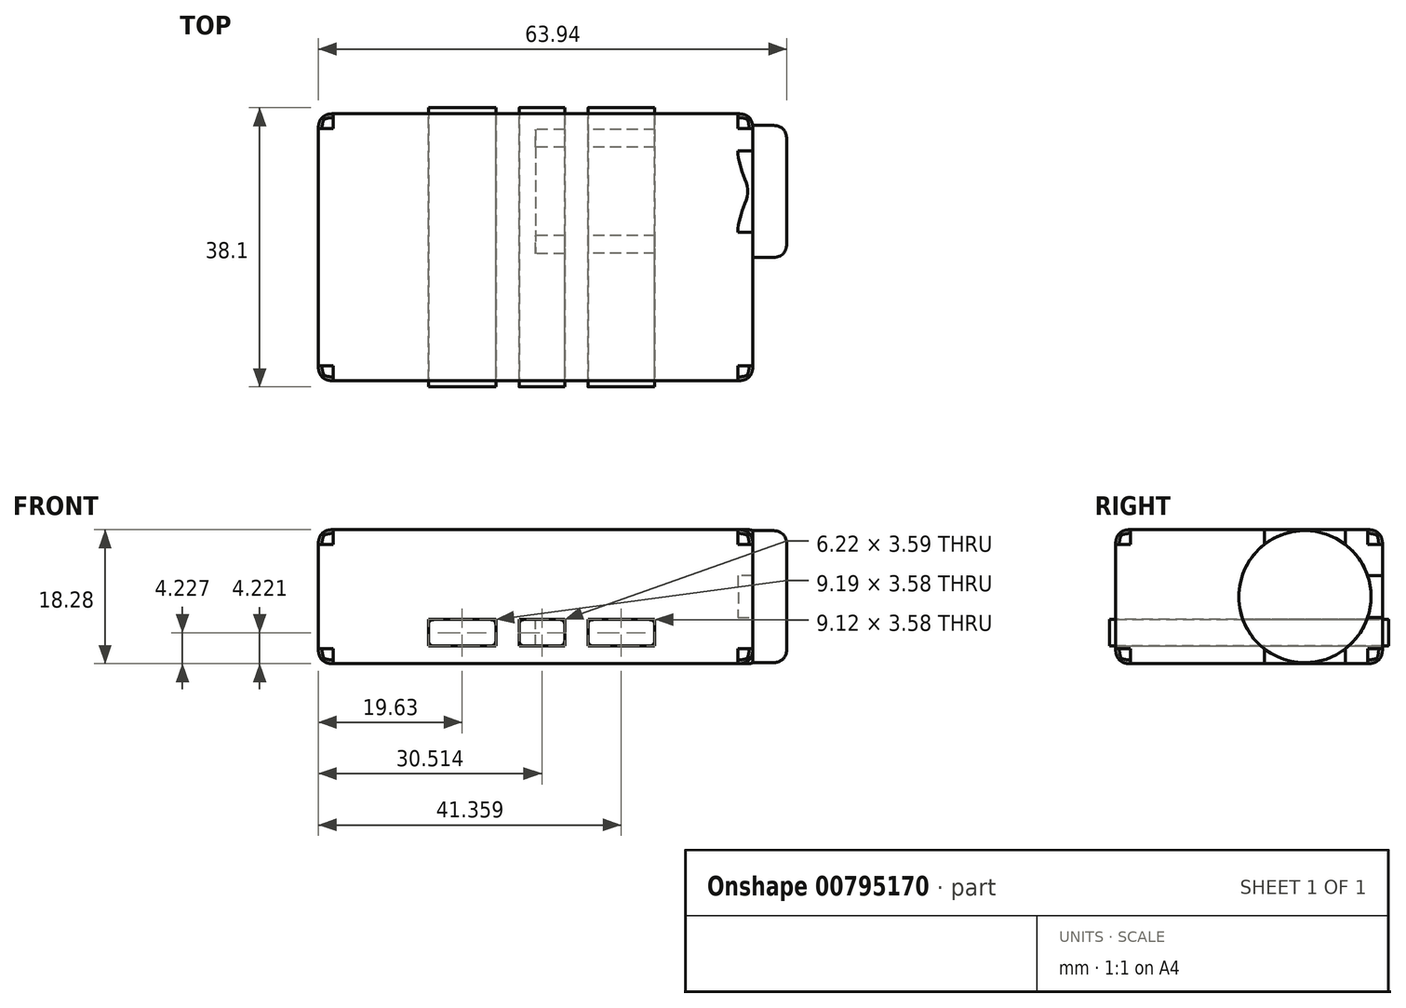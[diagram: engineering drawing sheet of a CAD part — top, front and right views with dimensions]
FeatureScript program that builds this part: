
annotation { "Feature Type Name" : "Feature", "Feature Type Description" : "" }
export const myFeature = defineFeature(function(context is Context, id is Id, definition is map)
    precondition{}
    {
        {
            var Q0;
            Q0=qCreatedBy(makeId("Front.planeOp"),FACE);
            var sketch = newSketch(context, id + "F0", { "sketchPlane" : qUnion([Q0])});
            skLineSegment(sketch, "E0.bottom", {"start": v(29.65, 9.14) * mm, "end": v(-29.65, 9.14) * mm});
            skLineSegment(sketch, "E0.top", {"start": v(29.65, -9.14) * mm, "end": v(-29.65, -9.14) * mm});
            skLineSegment(sketch, "E0.left", {"start": v(29.65, 9.14) * mm, "end": v(29.65, -9.14) * mm});
            skLineSegment(sketch, "E0.right", {"start": v(-29.65, 9.14) * mm, "end": v(-29.65, -9.14) * mm});
            skPoint(sketch, "E0.middle", {"position": v(0, 0) * mm});
            skLineSegment(sketch, "E1.left", {"start": v(29.65, 0) * mm, "end": v(29.65, 9.14) * mm});
            skLineSegment(sketch, "E2.bottom", {"start": v(7.15, -6.7) * mm, "end": v(16.27, -6.7) * mm});
            skLineSegment(sketch, "E2.top", {"start": v(7.15, -3.13) * mm, "end": v(16.27, -3.13) * mm});
            skLineSegment(sketch, "E2.left", {"start": v(7.15, -6.7) * mm, "end": v(7.15, -3.13) * mm});
            skLineSegment(sketch, "E2.right", {"start": v(16.27, -6.7) * mm, "end": v(16.27, -3.13) * mm});
            skLineSegment(sketch, "E3.left", {"start": v(7.15, -3.13) * mm, "end": v(7.15, -6.7) * mm});
            skLineSegment(sketch, "E4.bottom", {"start": v(3.98, -6.7) * mm, "end": v(-2.25, -6.7) * mm});
            skLineSegment(sketch, "E4.top", {"start": v(3.98, -3.12) * mm, "end": v(-2.25, -3.12) * mm});
            skLineSegment(sketch, "E4.left", {"start": v(3.98, -6.7) * mm, "end": v(3.98, -3.12) * mm});
            skLineSegment(sketch, "E4.right", {"start": v(-2.25, -6.7) * mm, "end": v(-2.25, -3.12) * mm});
            skLineSegment(sketch, "E5.bottom", {"start": v(-14.62, -6.7) * mm, "end": v(-5.42, -6.7) * mm});
            skLineSegment(sketch, "E5.top", {"start": v(-14.62, -3.13) * mm, "end": v(-5.42, -3.13) * mm});
            skLineSegment(sketch, "E5.left", {"start": v(-14.62, -6.7) * mm, "end": v(-14.62, -3.13) * mm});
            skLineSegment(sketch, "E5.right", {"start": v(-5.42, -6.7) * mm, "end": v(-5.42, -3.13) * mm});
            skSolve(sketch);
        }
        {
            var Q0;
            Q0=makeQuery(id+"F0.imprint","IMPRINT",FACE,{"disambiguationData":[TD([[makeQuery(id+"F0.imprint","IMPRINT",EDGE,{"derivedFrom":sQuery(id+"F0.wireOp",EDGE,"E0.bottom")}),1.0]])]});
            extrude(context, id + "F1", {"entities" : qUnion([Q0]), "endBound" : BoundingType.SYMMETRIC, "depth" : 36.42 * mm, "offsetDistance" : 25.4 * mm});
        }
        {
            var Q0;
            Q0=qCreatedBy(makeId("Right.planeOp"),FACE);
            var sketch = newSketch(context, id + "F2", { "sketchPlane" : qUnion([Q0])});
            skCircle(sketch, "E6", {"center": v(7.62, 0) * mm, "radius": 9.02 * mm});
            skSolve(sketch);
        }
        {
            var Q0;
            Q0 = qSketchRegion(id + "F2", true);
            extrude(context, id + "F3", {"entities" : qUnion([Q0]), "operationType" : NewBodyOperationType.ADD, "depth" : 34.3 * mm, "offsetDistance" : 25.4 * mm});
        }
        {
            var Q0;
            Q0=makeQuery(id+"F1.opExtrude","CAP_EDGE",EDGE,{"disambiguationData":[OSD([sQuery(id+"F0.wireOp",EDGE,"E0.bottom")])],"isStart":false});
            var Q1;
            Q1=makeQuery(id+"F1.opExtrude","CAP_EDGE",EDGE,{"disambiguationData":[OSD([sQuery(id+"F0.wireOp",EDGE,"E0.top")])],"isStart":false});
            var Q2;
            Q2=makeQuery(id+"F1.opExtrude","CAP_EDGE",EDGE,{"disambiguationData":[OSD([sQuery(id+"F0.wireOp",EDGE,"E0.left"),sQuery(id+"F0.wireOp",EDGE,"E1.left")])],"isStart":false});
            var Q3;
            Q3=makeQuery(id+"F1.opExtrude","SWEPT_EDGE",EDGE,{"disambiguationData":[OSD([sQuery(id+"F0.wireOp",EDGE,"E0.bottom"),sQuery(id+"F0.wireOp",EDGE,"E1.left")])]});
            var Q4;
            Q4=makeQuery(id+"F1.opExtrude","SWEPT_EDGE",EDGE,{"disambiguationData":[OSD([sQuery(id+"F0.wireOp",EDGE,"E0.top"),sQuery(id+"F0.wireOp",EDGE,"E0.left")])]});
            var Q5;
            Q5=makeQuery(id+"F1.opExtrude","CAP_EDGE",EDGE,{"disambiguationData":[OSD([sQuery(id+"F0.wireOp",EDGE,"E0.bottom")])],"isStart":true});
            var Q6;
            Q6=makeQuery(id+"F1.opExtrude","SWEPT_EDGE",EDGE,{"disambiguationData":[OSD([sQuery(id+"F0.wireOp",EDGE,"E0.bottom"),sQuery(id+"F0.wireOp",EDGE,"E0.right")])]});
            var Q7;
            Q7=makeQuery(id+"F1.opExtrude","SWEPT_EDGE",EDGE,{"disambiguationData":[OSD([sQuery(id+"F0.wireOp",EDGE,"E0.top"),sQuery(id+"F0.wireOp",EDGE,"E0.right")])]});
            var Q8;
            Q8=makeQuery(id+"F1.opExtrude","CAP_EDGE",EDGE,{"disambiguationData":[OSD([sQuery(id+"F0.wireOp",EDGE,"E0.right")])],"isStart":false});
            var Q9;
            Q9=makeQuery(id+"F1.opExtrude","CAP_EDGE",EDGE,{"disambiguationData":[OSD([sQuery(id+"F0.wireOp",EDGE,"E0.right")])],"isStart":true});
            var Q10;
            Q10=makeQuery(id+"F1.opExtrude","CAP_EDGE",EDGE,{"disambiguationData":[OSD([sQuery(id+"F0.wireOp",EDGE,"E0.top")])],"isStart":true});
            var Q11;
            Q11=makeQuery(id+"F1.opExtrude","CAP_EDGE",EDGE,{"disambiguationData":[OSD([sQuery(id+"F0.wireOp",EDGE,"E0.left"),sQuery(id+"F0.wireOp",EDGE,"E1.left")])],"isStart":true});
            var Q12;
            Q12=makeQuery(id+"F3.opExtrude","CAP_EDGE",EDGE,{"disambiguationData":[OSD([sQuery(id+"F2.wireOp",EDGE,"E6")])],"isStart":false});
            fillet(context, id + "F4", {"entities" : qUnion([Q0, Q1, Q2, Q3, Q4, Q5, Q6, Q7, Q8, Q9, Q10, Q11, Q12]), "radius" : 2.03 * mm, "tangentPropagation" : true, "rho" : 0.5, "crossSection" : FilletCrossSection.CONIC, "allowEdgeOverflow" : false});
        }
        {
            var Q0;
            Q0=makeQuery(id+"F0.imprint","IMPRINT",FACE,{"disambiguationData":[TD([[makeQuery(id+"F0.imprint","IMPRINT",EDGE,{"derivedFrom":sQuery(id+"F0.wireOp",EDGE,"E5.bottom")}),1.0]])]});
            var Q1;
            Q1=makeQuery(id+"F0.imprint","IMPRINT",FACE,{"disambiguationData":[TD([[makeQuery(id+"F0.imprint","IMPRINT",EDGE,{"derivedFrom":sQuery(id+"F0.wireOp",EDGE,"E4.bottom")}),-1.0]])]});
            var Q2;
            Q2=makeQuery(id+"F0.imprint","IMPRINT",FACE,{"disambiguationData":[TD([[makeQuery(id+"F0.imprint","IMPRINT",EDGE,{"derivedFrom":sQuery(id+"F0.wireOp",EDGE,"E2.bottom")}),1.0]])]});
            extrude(context, id + "F5", {"entities" : qUnion([Q0, Q1, Q2]), "endBound" : BoundingType.SYMMETRIC, "depth" : 38.1 * mm, "offsetDistance" : 25.4 * mm});
        }
        {
            var Q0;
            Q0=makeQuery(id+"F5.opExtrude","SWEPT_EDGE",EDGE,{"disambiguationData":[OSD([sQuery(id+"F0.wireOp",EDGE,"E5.top"),sQuery(id+"F0.wireOp",EDGE,"E5.left")])]});
            var Q1;
            Q1=makeQuery(id+"F5.opExtrude","SWEPT_EDGE",EDGE,{"disambiguationData":[OSD([sQuery(id+"F0.wireOp",EDGE,"E5.top"),sQuery(id+"F0.wireOp",EDGE,"E5.right")])]});
            var Q2;
            Q2=makeQuery(id+"F5.opExtrude","SWEPT_EDGE",EDGE,{"disambiguationData":[OSD([sQuery(id+"F0.wireOp",EDGE,"E5.bottom"),sQuery(id+"F0.wireOp",EDGE,"E5.right")])]});
            var Q3;
            Q3=makeQuery(id+"F5.opExtrude","SWEPT_EDGE",EDGE,{"disambiguationData":[OSD([sQuery(id+"F0.wireOp",EDGE,"E4.top"),sQuery(id+"F0.wireOp",EDGE,"E4.right")])]});
            var Q4;
            Q4=makeQuery(id+"F5.opExtrude","SWEPT_EDGE",EDGE,{"disambiguationData":[OSD([sQuery(id+"F0.wireOp",EDGE,"E4.top"),sQuery(id+"F0.wireOp",EDGE,"E4.left")])]});
            var Q5;
            Q5=makeQuery(id+"F5.opExtrude","SWEPT_EDGE",EDGE,{"disambiguationData":[OSD([sQuery(id+"F0.wireOp",EDGE,"E4.bottom"),sQuery(id+"F0.wireOp",EDGE,"E4.left")])]});
            var Q6;
            Q6=makeQuery(id+"F5.opExtrude","SWEPT_EDGE",EDGE,{"disambiguationData":[OSD([sQuery(id+"F0.wireOp",EDGE,"E2.top"),sQuery(id+"F0.wireOp",EDGE,"E3.left")])]});
            var Q7;
            Q7=makeQuery(id+"F5.opExtrude","SWEPT_EDGE",EDGE,{"disambiguationData":[OSD([sQuery(id+"F0.wireOp",EDGE,"E2.top"),sQuery(id+"F0.wireOp",EDGE,"E2.right")])]});
            var Q8;
            Q8=makeQuery(id+"F5.opExtrude","SWEPT_EDGE",EDGE,{"disambiguationData":[OSD([sQuery(id+"F0.wireOp",EDGE,"E2.bottom"),sQuery(id+"F0.wireOp",EDGE,"E2.right")])]});
            var Q9;
            Q9=makeQuery(id+"F5.opExtrude","SWEPT_EDGE",EDGE,{"disambiguationData":[OSD([sQuery(id+"F0.wireOp",EDGE,"E2.bottom"),sQuery(id+"F0.wireOp",EDGE,"E3.left")])]});
            var Q10;
            Q10=makeQuery(id+"F5.opExtrude","SWEPT_EDGE",EDGE,{"disambiguationData":[OSD([sQuery(id+"F0.wireOp",EDGE,"E4.bottom"),sQuery(id+"F0.wireOp",EDGE,"E4.right")])]});
            var Q11;
            Q11=makeQuery(id+"F5.opExtrude","SWEPT_EDGE",EDGE,{"disambiguationData":[OSD([sQuery(id+"F0.wireOp",EDGE,"E5.bottom"),sQuery(id+"F0.wireOp",EDGE,"E5.left")])]});
            fillet(context, id + "F6", {"entities" : qUnion([Q0, Q1, Q2, Q3, Q4, Q5, Q6, Q7, Q8, Q9, Q10, Q11]), "radius" : 0.76 * mm, "tangentPropagation" : true, "rho" : 0.5, "crossSection" : FilletCrossSection.CONIC, "allowEdgeOverflow" : false});
        }
    });
